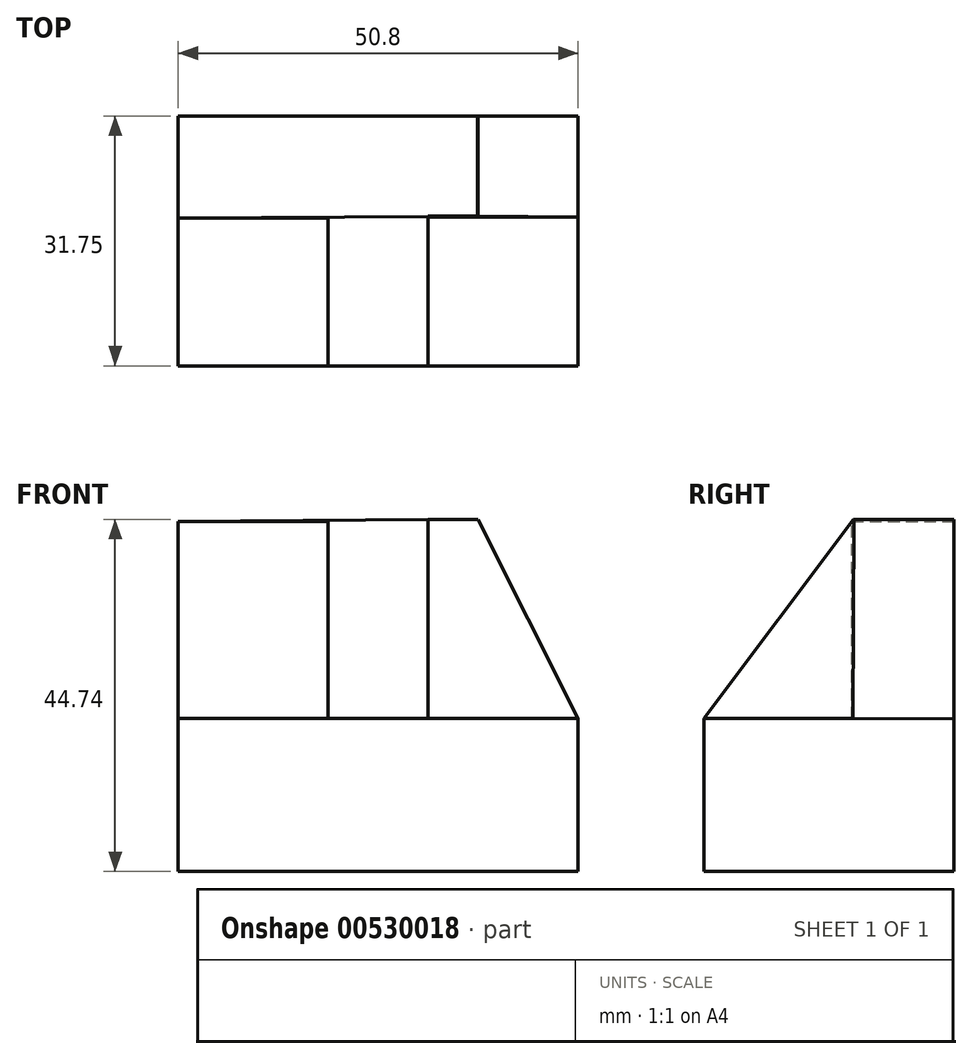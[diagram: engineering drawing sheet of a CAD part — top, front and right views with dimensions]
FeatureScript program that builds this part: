
annotation { "Feature Type Name" : "Feature", "Feature Type Description" : "" }
export const myFeature = defineFeature(function(context is Context, id is Id, definition is map)
    precondition{}
    {
        {
            var Q0;
            Q0=qCreatedBy(makeId("Front.planeOp"),FACE);
            var sketch = newSketch(context, id + "F0", { "sketchPlane" : qUnion([Q0])});
            skLineSegment(sketch, "E0", {"start": v(-65.9, 53.88) * mm, "end": v(-65.9, 9.43) * mm});
            skLineSegment(sketch, "E1", {"start": v(-65.9, 9.43) * mm, "end": v(-15.1, 9.43) * mm});
            skLineSegment(sketch, "E2", {"start": v(-15.1, 9.43) * mm, "end": v(-15.1, 54.27) * mm});
            skLineSegment(sketch, "E3", {"start": v(-65.9, 53.88) * mm, "end": v(-15.1, 54.27) * mm});
            skSolve(sketch);
        }
        {
            var Q0;
            Q0=makeQuery(id+"F0.imprint","IMPRINT",FACE,{"disambiguationData":[TD([[makeQuery(id+"F0.imprint","IMPRINT",EDGE,{"derivedFrom":sQuery(id+"F0.wireOp",EDGE,"E0")}),1.0]])]});
            extrude(context, id + "F1", {"entities" : qUnion([Q0]), "depth" : 31.75 * mm, "offsetDistance" : 25.4 * mm});
        }
        {
            var Q0;
            Q0=makeQuery(id+"F1.opExtrude","SWEPT_FACE",FACE,{"disambiguationData":[OSD([sQuery(id+"F0.wireOp",EDGE,"E2")])]});
            var sketch = newSketch(context, id + "F2", { "sketchPlane" : qUnion([Q0])});
            skLineSegment(sketch, "E4", {"start": v(-31.75, 54.27) * mm, "end": v(-31.75, 28.87) * mm});
            skLineSegment(sketch, "E5", {"start": v(-31.75, 54.27) * mm, "end": v(-12.7, 54.27) * mm});
            skLineSegment(sketch, "E6", {"start": v(-12.7, 54.27) * mm, "end": v(-31.75, 28.87) * mm});
            skSolve(sketch);
        }
        {
            var Q0;
            Q0=makeQuery(id+"F2.imprint","IMPRINT",FACE,{"disambiguationData":[TD([[makeQuery(id+"F2.imprint","IMPRINT",EDGE,{"derivedFrom":sQuery(id+"F2.wireOp",EDGE,"E4")}),-1.0]])]});
            extrude(context, id + "F3", {"entities" : qUnion([Q0]), "operationType" : NewBodyOperationType.REMOVE, "endBound" : BoundingType.THROUGH_ALL, "oppositeDirection" : true, "depth" : 25.4 * mm, "offsetDistance" : 25.4 * mm});
        }
        {
            var Q0;
            Q0=makeQuery(id+"F1.opExtrude","SWEPT_FACE",FACE,{"disambiguationData":[OSD([sQuery(id+"F0.wireOp",EDGE,"E2")])]});
            var sketch = newSketch(context, id + "F4", { "sketchPlane" : qUnion([Q0])});
            skLineSegment(sketch, "E7", {"start": v(-31.75, 28.87) * mm, "end": v(-12.84, 28.87) * mm});
            skLineSegment(sketch, "E8", {"start": v(-12.7, 54.27) * mm, "end": v(-12.84, 28.87) * mm});
            skLineSegment(sketch, "E9", {"start": v(-12.7, 54.27) * mm, "end": v(-31.75, 28.87) * mm});
            skSolve(sketch);
        }
        {
            var Q0;
            Q0=makeQuery(id+"F4.imprint","IMPRINT",FACE,{"disambiguationData":[TD([[makeQuery(id+"F4.imprint","IMPRINT",EDGE,{"derivedFrom":sQuery(id+"F4.wireOp",EDGE,"E7")}),1.0]])]});
            extrude(context, id + "F5", {"entities" : qUnion([Q0]), "operationType" : NewBodyOperationType.REMOVE, "oppositeDirection" : true, "depth" : 19.05 * mm, "offsetDistance" : 25.4 * mm});
        }
        {
            var Q0;
            Q0=makeQuery(id+"F1.opExtrude","SWEPT_FACE",FACE,{"disambiguationData":[OSD([sQuery(id+"F0.wireOp",EDGE,"E0")])]});
            var sketch = newSketch(context, id + "F6", { "sketchPlane" : qUnion([Q0])});
            skLineSegment(sketch, "E10", {"start": v(13, 53.88) * mm, "end": v(31.75, 28.87) * mm});
            skLineSegment(sketch, "E11", {"start": v(31.75, 28.87) * mm, "end": v(13, 28.87) * mm});
            skLineSegment(sketch, "E12", {"start": v(13, 28.87) * mm, "end": v(13, 53.88) * mm});
            skSolve(sketch);
        }
        {
            var Q0;
            Q0=makeQuery(id+"F6.imprint","IMPRINT",FACE,{"disambiguationData":[TD([[makeQuery(id+"F6.imprint","IMPRINT",EDGE,{"derivedFrom":sQuery(id+"F6.wireOp",EDGE,"E10")}),-1.0]])]});
            extrude(context, id + "F7", {"entities" : qUnion([Q0]), "operationType" : NewBodyOperationType.REMOVE, "oppositeDirection" : true, "depth" : 19.05 * mm, "offsetDistance" : 25.4 * mm});
        }
        {
            var Q0;
            Q0=makeQuery(id+"F5.boolean.opBoolean","COPY",FACE,{"derivedFrom":makeQuery(id+"F5.opExtrude","SWEPT_FACE",FACE,{"disambiguationData":[OSD([sQuery(id+"F4.wireOp",EDGE,"E8")])]})});
            var sketch = newSketch(context, id + "F8", { "sketchPlane" : qUnion([Q0])});
            skLineSegment(sketch, "E13", {"start": v(-15.1, 54.2) * mm, "end": v(-27.8, 54.1) * mm});
            skLineSegment(sketch, "E14", {"start": v(-27.8, 54.1) * mm, "end": v(-15.1, 28.8) * mm});
            skLineSegment(sketch, "E15", {"start": v(-15.1, 28.8) * mm, "end": v(-15.1, 54.2) * mm});
            skSolve(sketch);
        }
        {
            var Q0;
            Q0=makeQuery(id+"F1.opExtrude","SWEPT_FACE",FACE,{"disambiguationData":[OSD([sQuery(id+"F0.wireOp",EDGE,"E3")])]});
            var sketch = newSketch(context, id + "F9", { "sketchPlane" : qUnion([Q0])});
            skLineSegment(sketch, "E16", {"start": v(-27.44, -12.7) * mm, "end": v(-27.44, 0) * mm});
            skLineSegment(sketch, "E17", {"start": v(-27.44, 0) * mm, "end": v(-14.68, 0) * mm});
            skLineSegment(sketch, "E18", {"start": v(-14.68, 0) * mm, "end": v(-14.68, -12.7) * mm});
            skLineSegment(sketch, "E19", {"start": v(-27.44, -12.7) * mm, "end": v(-14.68, -12.7) * mm});
            skSolve(sketch);
        }
        {
            var Q0;
            Q0=makeQuery(id+"F8.imprint","IMPRINT",FACE,{"disambiguationData":[TD([[makeQuery(id+"F8.imprint","IMPRINT",EDGE,{"derivedFrom":sQuery(id+"F8.wireOp",EDGE,"E13")}),-1.0]])]});
            var Q1;
            Q1=makeQuery(id+"F9.imprint","IMPRINT",FACE,{"disambiguationData":[TD([[makeQuery(id+"F9.imprint","IMPRINT",EDGE,{"derivedFrom":sQuery(id+"F9.wireOp",EDGE,"E16")}),-1.0]])]});
            extrude(context, id + "F10", {"entities" : qUnion([Q0, Q1]), "operationType" : NewBodyOperationType.REMOVE, "oppositeDirection" : true, "depth" : 25.4 * mm, "offsetDistance" : 25.4 * mm});
        }
    });
